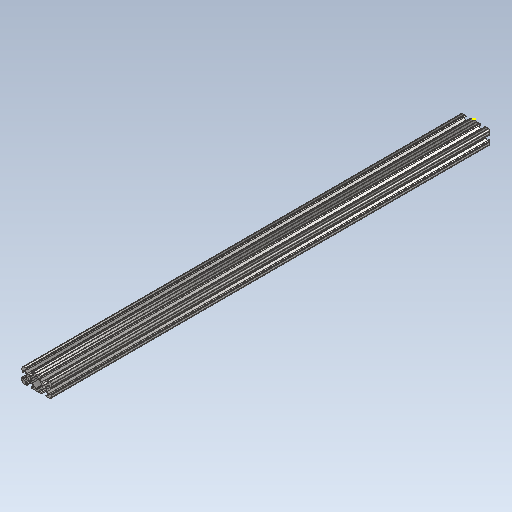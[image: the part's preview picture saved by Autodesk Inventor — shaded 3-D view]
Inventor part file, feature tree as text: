
AUTODESK INVENTOR PART (.ipt)
format: ipt  version: 2020 (Build 240168000, 168)  size: 387,072 bytes
history: native  units: in
note: dims shown in document units (in); Inventor stores cm internally (conversion verified against a paired STEP export)
features: other x3, sketch x2
ambient origin geometry x8: Origin, YZ Plane, XZ Plane, XY Plane, X Axis, Y Axis, Z Axis, Center Point
bodies: Solid1 (feature_tree)
feature tree (5):
  other  "25in 2x1 T Slot1.ipt"
  other  "Solid1::25in 2x1 T Slot1.ipt"
  other  "TaggingFeature1"
  sketch  "Sketch1"  dims[d0=0.3937in]
  sketch  "Sketch2"
